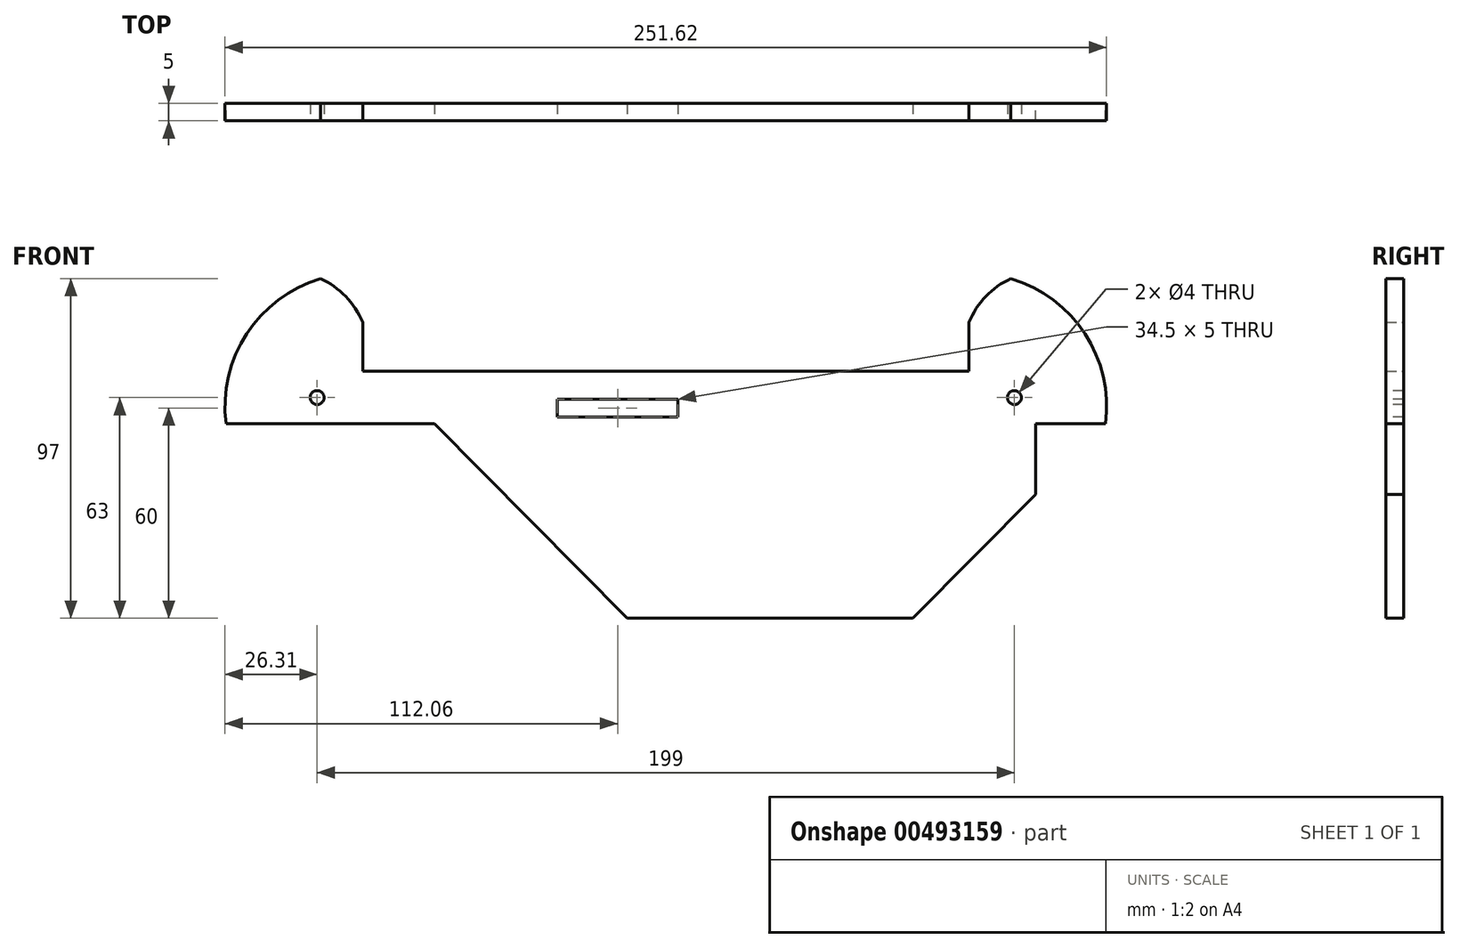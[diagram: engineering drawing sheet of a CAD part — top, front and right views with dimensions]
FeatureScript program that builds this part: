
annotation { "Feature Type Name" : "Feature", "Feature Type Description" : "" }
export const myFeature = defineFeature(function(context is Context, id is Id, definition is map)
    precondition{}
    {
        {
            var Q0;
            Q0=qCreatedBy(makeId("Front.planeOp"),FACE);
            var sketch = newSketch(context, id + "F0", { "sketchPlane" : qUnion([Q0])});
            skLineSegment(sketch, "E0.bottom", {"start": v(105.5, 35.25) * mm, "end": v(-105.5, 35.25) * mm, "construction": true});
            skLineSegment(sketch, "E0.top", {"start": v(105.5, -35.25) * mm, "end": v(-105.5, -35.25) * mm, "construction": true});
            skLineSegment(sketch, "E0.left", {"start": v(105.5, 35.25) * mm, "end": v(105.5, -35.25) * mm, "construction": true});
            skLineSegment(sketch, "E0.right", {"start": v(-105.5, 35.25) * mm, "end": v(-105.5, -35.25) * mm, "construction": true});
            skPoint(sketch, "E0.middle", {"position": v(0, 0) * mm});
            skLineSegment(sketch, "E1", {"start": v(-105.5, 35.25) * mm, "end": v(105.5, 35.25) * mm});
            skLineSegment(sketch, "E2", {"start": v(105.5, 35.25) * mm, "end": v(105.5, 20.25) * mm});
            skLineSegment(sketch, "E3", {"start": v(105.5, 20.25) * mm, "end": v(125.5, 20.25) * mm});
            skLineSegment(sketch, "E4", {"start": v(105.5, 35.25) * mm, "end": v(86.5, 35.25) * mm});
            skLineSegment(sketch, "E5", {"start": v(86.5, 35.25) * mm, "end": v(86.5, 49.25) * mm});
            skLineSegment(sketch, "E6", {"start": v(98.5, 35.25) * mm, "end": v(98.5, 61.75) * mm, "construction": true});
            skArc(sketch, "E7", {"start": v(98.5, 61.75) * mm, "mid": v(91.34, 56.6) * mm, "end": v(86.5, 49.25) * mm});
            skArc(sketch, "E8", {"start": v(125.5, 20.25) * mm, "mid": v(119.63, 45.96) * mm, "end": v(98.5, 61.75) * mm});
            skLineSegment(sketch, "E9", {"start": v(-105.5, 35.25) * mm, "end": v(-86.5, 35.25) * mm});
            skLineSegment(sketch, "E10", {"start": v(-86.5, 35.25) * mm, "end": v(-86.5, 49.25) * mm});
            skLineSegment(sketch, "E11", {"start": v(-105.5, 35.25) * mm, "end": v(-105.5, 20.25) * mm});
            skLineSegment(sketch, "E12", {"start": v(-105.5, 20.25) * mm, "end": v(-125.5, 20.25) * mm});
            skLineSegment(sketch, "E13", {"start": v(-98.5, 35.25) * mm, "end": v(-98.5, 61.75) * mm, "construction": true});
            skArc(sketch, "E14", {"start": v(-86.5, 49.25) * mm, "mid": v(-91.34, 56.6) * mm, "end": v(-98.5, 61.75) * mm});
            skArc(sketch, "E15", {"start": v(-98.5, 61.75) * mm, "mid": v(-119.63, 45.96) * mm, "end": v(-125.5, 20.25) * mm});
            skLineSegment(sketch, "E16", {"start": v(-105.5, 20.25) * mm, "end": v(-105.5, -35.25) * mm});
            skLineSegment(sketch, "E17", {"start": v(105.5, 20.25) * mm, "end": v(105.5, -35.25) * mm});
            skLineSegment(sketch, "E18", {"start": v(105.5, -35.25) * mm, "end": v(-105.5, -35.25) * mm});
            skSolve(sketch);
        }
        {
            var Q0;
            Q0 = qSketchRegion(id + "F0", true);
            extrude(context, id + "F1", {"entities" : qUnion([Q0]), "depth" : 5 * mm});
        }
        {
            var Q0;
            Q0=makeQuery(id+"F1.opExtrude","CAP_FACE",FACE,{"disambiguationData":[OSD([sQuery(id+"F0.wireOp",EDGE,"E1"),sQuery(id+"F0.wireOp",EDGE,"E3"),sQuery(id+"F0.wireOp",EDGE,"E5"),sQuery(id+"F0.wireOp",EDGE,"E7"),sQuery(id+"F0.wireOp",EDGE,"E8"),sQuery(id+"F0.wireOp",EDGE,"E10"),sQuery(id+"F0.wireOp",EDGE,"E12"),sQuery(id+"F0.wireOp",EDGE,"E14"),sQuery(id+"F0.wireOp",EDGE,"E15"),sQuery(id+"F0.wireOp",EDGE,"E16"),sQuery(id+"F0.wireOp",EDGE,"E17"),sQuery(id+"F0.wireOp",EDGE,"E18")])],"isStart":false});
            var sketch = newSketch(context, id + "F2", { "sketchPlane" : qUnion([Q0])});
            skLineSegment(sketch, "E19.bottom", {"start": v(-11, -35.25) * mm, "end": v(70.5, -35.25) * mm, "construction": true});
            skLineSegment(sketch, "E19.left", {"start": v(-11, -35.25) * mm, "end": v(-11, -11.04) * mm, "construction": true});
            skLineSegment(sketch, "E19.right", {"start": v(70.5, -35.25) * mm, "end": v(70.5, -11.04) * mm, "construction": true});
            skLineSegment(sketch, "E20", {"start": v(-105.5, 20.25) * mm, "end": v(-11, 20.25) * mm, "construction": true});
            skLineSegment(sketch, "E21", {"start": v(-11, -11.04) * mm, "end": v(-11, 20.25) * mm, "construction": true});
            skLineSegment(sketch, "E22", {"start": v(70.5, -11.04) * mm, "end": v(70.5, 20.25) * mm, "construction": true});
            skLineSegment(sketch, "E23", {"start": v(70.5, 20.25) * mm, "end": v(105.5, 20.25) * mm, "construction": true});
            skLineSegment(sketch, "E24", {"start": v(70.5, -35.25) * mm, "end": v(125.5, 20.25) * mm});
            skLineSegment(sketch, "E25", {"start": v(125.5, 20.25) * mm, "end": v(119.7, -35.25) * mm});
            skLineSegment(sketch, "E26", {"start": v(119.7, -35.25) * mm, "end": v(70.5, -35.25) * mm});
            skLineSegment(sketch, "E27", {"start": v(-11, -35.25) * mm, "end": v(-66.02, 20.25) * mm});
            skLineSegment(sketch, "E28", {"start": v(-66.02, 20.25) * mm, "end": v(-105.5, 20.25) * mm});
            skLineSegment(sketch, "E29", {"start": v(-105.5, 20.25) * mm, "end": v(-105.5, -35.25) * mm});
            skLineSegment(sketch, "E30", {"start": v(-105.5, -35.25) * mm, "end": v(-11, -35.25) * mm});
            skLineSegment(sketch, "E31.bottom", {"start": v(-31, 27.25) * mm, "end": v(3.5, 27.25) * mm});
            skLineSegment(sketch, "E31.top", {"start": v(-31, 22.25) * mm, "end": v(3.5, 22.25) * mm});
            skLineSegment(sketch, "E31.left", {"start": v(-31, 27.25) * mm, "end": v(-31, 22.25) * mm});
            skLineSegment(sketch, "E31.right", {"start": v(3.5, 27.25) * mm, "end": v(3.5, 22.25) * mm});
            skSolve(sketch);
        }
        {
            var Q0;
            Q0 = qSketchRegion(id + "F2", true);
            extrude(context, id + "F3", {"entities" : qUnion([Q0]), "operationType" : NewBodyOperationType.REMOVE, "oppositeDirection" : true, "depth" : 25 * mm});
        }
        {
            var Q0;
            Q0=makeQuery(id+"F1.opExtrude","CAP_FACE",FACE,{"disambiguationData":[OSD([sQuery(id+"F0.wireOp",EDGE,"E1"),sQuery(id+"F0.wireOp",EDGE,"E3"),sQuery(id+"F0.wireOp",EDGE,"E5"),sQuery(id+"F0.wireOp",EDGE,"E7"),sQuery(id+"F0.wireOp",EDGE,"E8"),sQuery(id+"F0.wireOp",EDGE,"E10"),sQuery(id+"F0.wireOp",EDGE,"E12"),sQuery(id+"F0.wireOp",EDGE,"E14"),sQuery(id+"F0.wireOp",EDGE,"E15"),sQuery(id+"F0.wireOp",EDGE,"E16"),sQuery(id+"F0.wireOp",EDGE,"E17"),sQuery(id+"F0.wireOp",EDGE,"E18")])],"isStart":false});
            var sketch = newSketch(context, id + "F4", { "sketchPlane" : qUnion([Q0])});
            skCircle(sketch, "E32", {"center": v(-99.5, 27.75) * mm, "radius": 2 * mm});
            skCircle(sketch, "E33", {"center": v(99.5, 27.75) * mm, "radius": 2 * mm});
            skLineSegment(sketch, "E34", {"start": v(-125.5, 20.25) * mm, "end": v(-125.5, 44.77) * mm, "construction": true});
            skLineSegment(sketch, "E35", {"start": v(125.5, 20.25) * mm, "end": v(125.5, 60.63) * mm, "construction": true});
            skSolve(sketch);
        }
        {
            var Q0;
            Q0 = qSketchRegion(id + "F4", true);
            extrude(context, id + "F5", {"entities" : qUnion([Q0]), "operationType" : NewBodyOperationType.REMOVE, "oppositeDirection" : true, "depth" : 25 * mm});
        }
    });
